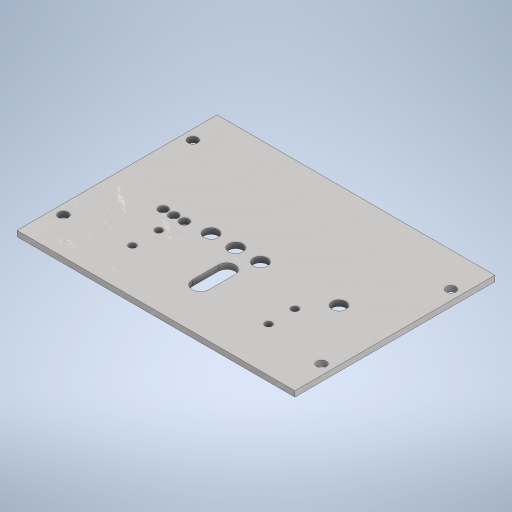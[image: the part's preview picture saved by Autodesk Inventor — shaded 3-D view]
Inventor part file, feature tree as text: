
AUTODESK INVENTOR PART (.ipt)
format: ipt  version: 2023 (Build 270158000, 158)  size: 439,296 bytes
history: native  units: mm
features: reference x19, extrude x12, sketch x12, other x7, projected_geometry x3
ambient origin geometry x8: Origin, YZ Plane, XZ Plane, XY Plane, X Axis, Y Axis, Z Axis, Center Point
bodies: Body1 (feature_tree)
feature tree (53):
  other  "Bryła1"
  extrude  "Wyciągnięcie proste1"  Depth=100.0mm
  extrude  "Wyciągnięcie proste2"  Depth=70.0mm
  extrude  "Wyciągnięcie proste3"  Depth=0.5mm TaperAngle=0.0deg
  extrude  "Wyciągnięcie proste4"  Depth=0.5mm
  extrude  "Wyciągnięcie proste5"  Depth=0.5mm
  extrude  "Wyciągnięcie proste6"  Depth=0.5mm
  extrude  "Wyciągnięcie proste7"  Depth=0.5mm
  extrude  "Wyciągnięcie proste8"  Depth=1.3mm
  extrude  "Wyciągnięcie proste9"  TaperAngle=0.0deg  [1 undecoded]
  extrude  "Wyciągnięcie proste10"  TaperAngle=0.0deg  [1 undecoded]
  extrude  "Wyciągnięcie proste11"  Depth=1.2mm TaperAngle=0.0deg
  extrude  "Wyciągnięcie proste12"  Depth=3.5mm
  sketch  "Szkic1"
  sketch  "Szkic2"
  reference  "Odniesienie1"
  reference  "Odniesienie2"
  reference  "Odniesienie3"
  reference  "Odniesienie4"
  reference  "Odniesienie5"
  reference  "Odniesienie6"
  reference  "Odniesienie7"
  reference  "Odniesienie8"
  reference  "Odniesienie9"
  sketch  "Szkic3"
  reference  "Odniesienie10"
  reference  "Odniesienie11"
  reference  "Odniesienie12"
  reference  "Odniesienie13"
  reference  "Odniesienie14"
  reference  "Odniesienie15"
  reference  "Odniesienie16"
  reference  "Odniesienie17"
  reference  "Odniesienie18"
  reference  "Odniesienie19"
  sketch  "Szkic4"
  projected_geometry  "Pętla rzutowana1"
  sketch  "Szkic5"
  projected_geometry  "Pętla rzutowana2"
  sketch  "Szkic6"
  sketch  "Szkic7"
  projected_geometry  "Pętla rzutowana3"
  sketch  "Szkic8"
  sketch  "Szkic9"
  sketch  "Szkic10"
  sketch  "Szkic11"
  sketch  "Szkic12"
  other  "<userpath>\Desktop\MojeRoboty\Stefan\mechanics 2\STEFAN.iam"
  other  "STEFAN.iam"
  other  "board_up:1"
  other  "sciana_prawa_nowa_MIR:1"
  other  "sciana_prawa_nowa:1"
  other  "uchwyt_serw:1"
note: 2 required parameter values undecoded (feature->parameter linkage not recoverable at this tier; creation-order binding heuristic only, values carry confidence <= 0.55)
